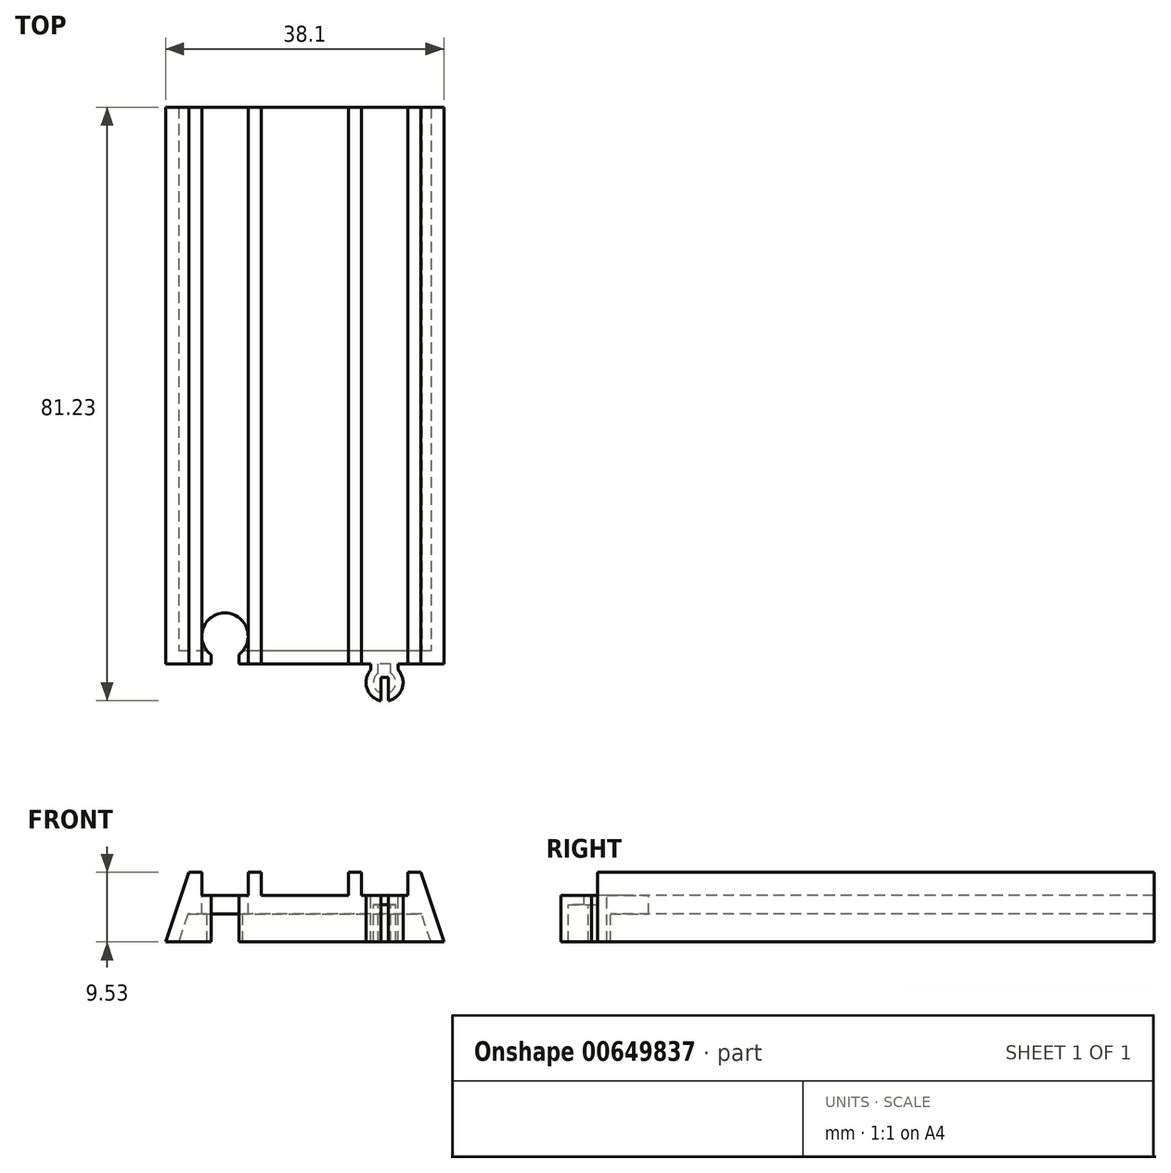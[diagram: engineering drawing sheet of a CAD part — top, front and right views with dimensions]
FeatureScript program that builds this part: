
annotation { "Feature Type Name" : "Feature", "Feature Type Description" : "" }
export const myFeature = defineFeature(function(context is Context, id is Id, definition is map)
    precondition{}
    {
        {
            var Q0;
            Q0=qCreatedBy(makeId("Front.planeOp"),FACE);
            var sketch = newSketch(context, id + "F0", { "sketchPlane" : qUnion([Q0])});
            skLineSegment(sketch, "E0", {"start": v(-19.05, 0) * mm, "end": v(-15.88, 9.52) * mm});
            skLineSegment(sketch, "E1", {"start": v(-15.88, 9.52) * mm, "end": v(15.88, 9.53) * mm});
            skLineSegment(sketch, "E2", {"start": v(15.88, 9.52) * mm, "end": v(19.05, 0) * mm});
            skLineSegment(sketch, "E3", {"start": v(19.05, 0) * mm, "end": v(-19.05, 0) * mm});
            skSolve(sketch);
        }
        {
            var Q0;
            Q0 = qSketchRegion(id + "F0", true);
            extrude(context, id + "F1", {"entities" : qUnion([Q0]), "depth" : 76.2 * mm, "offsetDistance" : 25.4 * mm});
        }
        {
            var Q0;
            Q0=makeQuery(id+"F1.opExtrude","CAP_FACE",FACE,{"disambiguationData":[OSD([sQuery(id+"F0.wireOp",EDGE,"E0"),sQuery(id+"F0.wireOp",EDGE,"E1"),sQuery(id+"F0.wireOp",EDGE,"E2"),sQuery(id+"F0.wireOp",EDGE,"E3")])],"isStart":false});
            var sketch = newSketch(context, id + "F2", { "sketchPlane" : qUnion([Q0])});
            skLineSegment(sketch, "E4.bottom", {"start": v(-14.1, 9.52) * mm, "end": v(-7.75, 9.52) * mm});
            skLineSegment(sketch, "E4.top", {"start": v(-14.1, 6.35) * mm, "end": v(-7.75, 6.35) * mm});
            skLineSegment(sketch, "E4.left", {"start": v(-14.1, 9.52) * mm, "end": v(-14.1, 6.35) * mm});
            skLineSegment(sketch, "E4.right", {"start": v(-7.75, 9.52) * mm, "end": v(-7.75, 6.35) * mm});
            skLineSegment(sketch, "E5.bottom", {"start": v(7.75, 9.52) * mm, "end": v(14.1, 9.52) * mm});
            skLineSegment(sketch, "E5.top", {"start": v(7.75, 6.35) * mm, "end": v(14.1, 6.35) * mm});
            skLineSegment(sketch, "E5.left", {"start": v(7.75, 9.52) * mm, "end": v(7.75, 6.35) * mm});
            skLineSegment(sketch, "E5.right", {"start": v(14.1, 9.52) * mm, "end": v(14.1, 6.35) * mm});
            skPoint(sketch, "E6", {"position": v(-15.88, 9.52) * mm});
            skLineSegment(sketch, "E7.bottom", {"start": v(-5.97, 9.52) * mm, "end": v(5.97, 9.52) * mm});
            skLineSegment(sketch, "E7.top", {"start": v(-5.97, 6.35) * mm, "end": v(5.97, 6.35) * mm});
            skLineSegment(sketch, "E7.left", {"start": v(-5.97, 9.52) * mm, "end": v(-5.97, 6.35) * mm});
            skLineSegment(sketch, "E7.right", {"start": v(5.97, 9.52) * mm, "end": v(5.97, 6.35) * mm});
            skPoint(sketch, "E8", {"position": v(15.88, 9.53) * mm});
            skLineSegment(sketch, "E9", {"start": v(-17.27, 0) * mm, "end": v(-16, 3.8) * mm});
            skLineSegment(sketch, "E10", {"start": v(-16, 3.8) * mm, "end": v(16, 3.8) * mm});
            skLineSegment(sketch, "E11", {"start": v(16, 3.8) * mm, "end": v(17.27, 0) * mm});
            skLineSegment(sketch, "E12", {"start": v(17.27, 0) * mm, "end": v(-17.27, 0) * mm});
            skLineSegment(sketch, "E13", {"start": v(-15.88, 9.52) * mm, "end": v(-14.1, 9.52) * mm, "construction": true});
            skLineSegment(sketch, "E14", {"start": v(-7.75, 9.52) * mm, "end": v(-5.97, 9.52) * mm});
            skLineSegment(sketch, "E15", {"start": v(5.97, 9.52) * mm, "end": v(7.75, 9.52) * mm});
            skLineSegment(sketch, "E16", {"start": v(14.1, 9.52) * mm, "end": v(15.88, 9.52) * mm});
            skLineSegment(sketch, "E17", {"start": v(-17.27, 0) * mm, "end": v(-19.05, 0) * mm, "construction": true});
            skLineSegment(sketch, "E18", {"start": v(17.27, 0) * mm, "end": v(19.05, 0) * mm, "construction": true});
            skSolve(sketch);
        }
        {
            var Q0;
            Q0 = qSketchRegion(id + "F2", true);
            extrude(context, id + "F3", {"entities" : qUnion([Q0]), "operationType" : NewBodyOperationType.REMOVE, "endBound" : BoundingType.THROUGH_ALL, "oppositeDirection" : true, "depth" : 25.4 * mm, "offsetDistance" : 25.4 * mm});
        }
        {
            var Q0;
            Q0=makeQuery(id+"F1.opExtrude","CAP_FACE",FACE,{"disambiguationData":[OSD([sQuery(id+"F0.wireOp",EDGE,"E0"),sQuery(id+"F0.wireOp",EDGE,"E1"),sQuery(id+"F0.wireOp",EDGE,"E2"),sQuery(id+"F0.wireOp",EDGE,"E3")])],"isStart":false});
            var sketch = newSketch(context, id + "F4", { "sketchPlane" : qUnion([Q0])});
            skLineSegment(sketch, "E19", {"start": v(-19.05, 0) * mm, "end": v(-15.88, 9.52) * mm});
            skLineSegment(sketch, "E20", {"start": v(-15.88, 9.52) * mm, "end": v(-14.1, 9.52) * mm});
            skLineSegment(sketch, "E21", {"start": v(15.88, 9.52) * mm, "end": v(19.05, 0) * mm});
            skLineSegment(sketch, "E22", {"start": v(19.05, 0) * mm, "end": v(-19.05, 0) * mm});
            skLineSegment(sketch, "E23", {"start": v(-14.1, 9.52) * mm, "end": v(-14.1, 6.35) * mm});
            skLineSegment(sketch, "E24", {"start": v(-14.1, 6.35) * mm, "end": v(-7.75, 6.35) * mm});
            skLineSegment(sketch, "E25", {"start": v(-7.75, 6.35) * mm, "end": v(-7.75, 9.52) * mm});
            skLineSegment(sketch, "E26.trimOffspring", {"start": v(-7.75, 9.52) * mm, "end": v(-5.97, 9.52) * mm});
            skLineSegment(sketch, "E27.bottom", {"start": v(7.75, 6.35) * mm, "end": v(14.1, 6.35) * mm});
            skLineSegment(sketch, "E27.left", {"start": v(7.75, 6.35) * mm, "end": v(7.75, 9.52) * mm});
            skLineSegment(sketch, "E27.right", {"start": v(14.1, 6.35) * mm, "end": v(14.1, 9.53) * mm});
            skLineSegment(sketch, "E28.trimOffspring", {"start": v(14.1, 9.53) * mm, "end": v(15.88, 9.53) * mm});
            skLineSegment(sketch, "E29", {"start": v(-5.97, 6.35) * mm, "end": v(5.97, 6.35) * mm});
            skLineSegment(sketch, "E30", {"start": v(5.97, 6.35) * mm, "end": v(5.97, 9.52) * mm});
            skLineSegment(sketch, "E31", {"start": v(5.97, 9.52) * mm, "end": v(7.75, 9.52) * mm});
            skLineSegment(sketch, "E32", {"start": v(-5.97, 9.52) * mm, "end": v(-5.97, 6.35) * mm});
            skSolve(sketch);
        }
        {
            var Q0;
            Q0 = qSketchRegion(id + "F4", true);
            extrude(context, id + "F5", {"entities" : qUnion([Q0]), "operationType" : NewBodyOperationType.ADD, "oppositeDirection" : true, "depth" : 1.78 * mm, "offsetDistance" : 25.4 * mm});
        }
        {
            var Q0;
            Q0=makeQuery(id+"F3.boolean.opBoolean","COPY",FACE,{"derivedFrom":makeQuery(id+"F3.opExtrude","SWEPT_FACE",FACE,{"disambiguationData":[OSD([sQuery(id+"F2.wireOp",EDGE,"E10")])]})});
            var sketch = newSketch(context, id + "F6", { "sketchPlane" : qUnion([Q0])});
            skArc(sketch, "E33", {"start": v(-13.36, 74.42) * mm, "mid": v(-10.92, 69.22) * mm, "end": v(-8.48, 74.42) * mm});
            skLineSegment(sketch, "E34", {"start": v(-10.92, 76.2) * mm, "end": v(-10.92, 72.4) * mm, "construction": true});
            skSolve(sketch);
        }
        {
            var Q0;
            Q0=makeQuery(id+"F6.imprint","IMPRINT",FACE,{"disambiguationData":[TD([[makeQuery(id+"F6.imprint","IMPRINT",EDGE,{"derivedFrom":sQuery(id+"F6.wireOp",EDGE,"E33")}),1.0]])]});
            var Q1;
            {var subQ0=sQuery(id+"F0.wireOp",EDGE,"E3");var subQ1=sQuery(id+"F0.wireOp",EDGE,"E2");var subQ3=sQuery(id+"F0.wireOp",EDGE,"E0");var subQ6=makeQuery(id+"F1.opExtrude","SWEPT_FACE",FACE,{"disambiguationData":[OSD([subQ0])]});Q1=makeQuery(id+"F5.boolean.opBoolean","MERGE",FACE,{"derivedFrom":[makeQuery(id+"F3.boolean.opBoolean","SPLIT",FACE,{"disambiguationData":[TD([makeQuery(id+"F1.opExtrude","SWEPT_FACE",FACE,{"disambiguationData":[OSD([subQ3])]})])],"derivedFrom":subQ6}),makeQuery(id+"F3.boolean.opBoolean","SPLIT",FACE,{"disambiguationData":[TD([makeQuery(id+"F1.opExtrude","SWEPT_FACE",FACE,{"disambiguationData":[OSD([subQ1])]})])],"derivedFrom":subQ6}),makeQuery(id+"F5.opExtrude","SWEPT_FACE",FACE,{"disambiguationData":[OSD([sQuery(id+"F4.wireOp",EDGE,"E22")])]})]});}
            extrude(context, id + "F7", {"entities" : qUnion([Q0]), "operationType" : NewBodyOperationType.ADD, "endBound" : BoundingType.UP_TO_SURFACE, "depth" : 25.4 * mm, "endBoundEntityFace" : qUnion([Q1]), "offsetDistance" : 25.4 * mm});
        }
        {
            var Q0;
            Q0=makeQuery(id+"F3.boolean.opBoolean","COPY",FACE,{"derivedFrom":makeQuery(id+"F3.opExtrude","SWEPT_FACE",FACE,{"disambiguationData":[OSD([sQuery(id+"F2.wireOp",EDGE,"E4.top")])]})});
            var sketch = newSketch(context, id + "F8", { "sketchPlane" : qUnion([Q0])});
            skArc(sketch, "E35", {"start": v(-9.02, -74.93) * mm, "mid": v(-10.92, -69.22) * mm, "end": v(-12.83, -74.93) * mm});
            skLineSegment(sketch, "E36", {"start": v(-12.83, -74.93) * mm, "end": v(-12.83, -76.2) * mm});
            skLineSegment(sketch, "E37", {"start": v(-9.02, -74.93) * mm, "end": v(-9.02, -76.2) * mm});
            skLineSegment(sketch, "E38", {"start": v(-9.02, -76.2) * mm, "end": v(-12.83, -76.2) * mm});
            skLineSegment(sketch, "E39", {"start": v(-9.02, -76.2) * mm, "end": v(-7.75, -76.2) * mm, "construction": true});
            skLineSegment(sketch, "E40", {"start": v(-12.83, -76.2) * mm, "end": v(-14.1, -76.2) * mm, "construction": true});
            skSolve(sketch);
        }
        {
            var Q0;
            Q0 = qSketchRegion(id + "F8", true);
            extrude(context, id + "F9", {"entities" : qUnion([Q0]), "operationType" : NewBodyOperationType.REMOVE, "endBound" : BoundingType.THROUGH_ALL, "oppositeDirection" : true, "depth" : 25.4 * mm, "offsetDistance" : 25.4 * mm});
        }
        {
            var Q0;
            Q0=makeQuery(id+"F3.boolean.opBoolean","COPY",FACE,{"derivedFrom":makeQuery(id+"F3.opExtrude","SWEPT_FACE",FACE,{"disambiguationData":[OSD([sQuery(id+"F2.wireOp",EDGE,"E5.top")])]})});
            var sketch = newSketch(context, id + "F10", { "sketchPlane" : qUnion([Q0])});
            skArc(sketch, "E41", {"start": v(9.04, -77.04) * mm, "mid": v(8.5, -79.53) * mm, "end": v(10.41, -81.23) * mm});
            skLineSegment(sketch, "E42", {"start": v(10.92, -76.2) * mm, "end": v(10.92, -78.74) * mm, "construction": true});
            skLineSegment(sketch, "E43", {"start": v(9.04, -77.04) * mm, "end": v(9.04, -76.2) * mm});
            skLineSegment(sketch, "E44", {"start": v(9.04, -76.2) * mm, "end": v(12.8, -76.2) * mm});
            skLineSegment(sketch, "E45", {"start": v(12.8, -76.2) * mm, "end": v(12.8, -77.04) * mm});
            skLineSegment(sketch, "E46", {"start": v(10.41, -81.23) * mm, "end": v(10.41, -78.05) * mm});
            skLineSegment(sketch, "E47", {"start": v(10.41, -78.05) * mm, "end": v(11.43, -78.05) * mm});
            skLineSegment(sketch, "E48", {"start": v(11.43, -78.05) * mm, "end": v(11.43, -81.23) * mm});
            skArc(sketch, "E49.trimOffspring", {"start": v(11.43, -81.23) * mm, "mid": v(13.34, -79.53) * mm, "end": v(12.8, -77.04) * mm});
            skSolve(sketch);
        }
        {
            var Q0;
            Q0=makeQuery(id+"F10.imprint","IMPRINT",FACE,{"disambiguationData":[TD([[makeQuery(id+"F10.imprint","IMPRINT",EDGE,{"derivedFrom":sQuery(id+"F10.wireOp",EDGE,"E41")}),1.0]])]});
            extrude(context, id + "F11", {"entities" : qUnion([Q0]), "operationType" : NewBodyOperationType.ADD, "oppositeDirection" : true, "depth" : 1.27 * mm, "offsetDistance" : 25.4 * mm});
        }
        {
            var Q0;
            Q0=makeQuery(id+"F11.opExtrude","CAP_FACE",FACE,{"disambiguationData":[OSD([sQuery(id+"F10.wireOp",EDGE,"E41"),sQuery(id+"F10.wireOp",EDGE,"E43"),sQuery(id+"F10.wireOp",EDGE,"E44"),sQuery(id+"F10.wireOp",EDGE,"E45"),sQuery(id+"F10.wireOp",EDGE,"E46"),sQuery(id+"F10.wireOp",EDGE,"E47"),sQuery(id+"F10.wireOp",EDGE,"E48"),sQuery(id+"F10.wireOp",EDGE,"E49.trimOffspring")])],"isStart":false});
            var sketch = newSketch(context, id + "F12", { "sketchPlane" : qUnion([Q0])});
            skArc(sketch, "E50", {"start": v(12.8, 77.04) * mm, "mid": v(13.34, 79.53) * mm, "end": v(11.43, 81.23) * mm});
            skLineSegment(sketch, "E51", {"start": v(9.04, 77.04) * mm, "end": v(9.04, 76.2) * mm});
            skLineSegment(sketch, "E52", {"start": v(9.04, 76.2) * mm, "end": v(10.05, 76.2) * mm});
            skLineSegment(sketch, "E53", {"start": v(12.8, 76.2) * mm, "end": v(12.8, 77.04) * mm});
            skArc(sketch, "E54", {"start": v(11.79, 77.49) * mm, "mid": v(12.43, 78.94) * mm, "end": v(11.43, 80.18) * mm});
            skLineSegment(sketch, "E55", {"start": v(10.05, 77.49) * mm, "end": v(10.05, 76.2) * mm});
            skLineSegment(sketch, "E56", {"start": v(11.79, 77.49) * mm, "end": v(11.79, 76.2) * mm});
            skLineSegment(sketch, "E57.trimOffspring", {"start": v(11.79, 76.2) * mm, "end": v(12.8, 76.2) * mm});
            skLineSegment(sketch, "E58", {"start": v(10.41, 81.23) * mm, "end": v(10.41, 80.18) * mm});
            skLineSegment(sketch, "E59", {"start": v(11.43, 81.23) * mm, "end": v(11.43, 80.18) * mm});
            skArc(sketch, "E60.trimOffspring", {"start": v(10.41, 80.18) * mm, "mid": v(9.41, 78.94) * mm, "end": v(10.05, 77.49) * mm});
            skArc(sketch, "E61.trimOffspring", {"start": v(10.41, 81.23) * mm, "mid": v(8.5, 79.53) * mm, "end": v(9.04, 77.04) * mm});
            skSolve(sketch);
        }
        {
            var Q0;
            Q0 = qSketchRegion(id + "F12", true);
            var Q1;
            {var subQ0=sQuery(id+"F4.wireOp",EDGE,"E22");var subQ1=sQuery(id+"F0.wireOp",EDGE,"E3");var subQ2=sQuery(id+"F0.wireOp",EDGE,"E2");var subQ4=sQuery(id+"F0.wireOp",EDGE,"E0");var subQ7=makeQuery(id+"F1.opExtrude","SWEPT_FACE",FACE,{"disambiguationData":[OSD([subQ1])]});Q1=makeQuery(id+"F7.boolean.opBoolean","MERGE",FACE,{"derivedFrom":[makeQuery(id+"F5.boolean.opBoolean","MERGE",FACE,{"derivedFrom":[makeQuery(id+"F3.boolean.opBoolean","SPLIT",FACE,{"disambiguationData":[TD([makeQuery(id+"F1.opExtrude","SWEPT_FACE",FACE,{"disambiguationData":[OSD([subQ4])]})])],"derivedFrom":subQ7}),makeQuery(id+"F3.boolean.opBoolean","SPLIT",FACE,{"disambiguationData":[TD([makeQuery(id+"F1.opExtrude","SWEPT_FACE",FACE,{"disambiguationData":[OSD([subQ2])]})])],"derivedFrom":subQ7}),makeQuery(id+"F5.opExtrude","SWEPT_FACE",FACE,{"disambiguationData":[OSD([subQ0])]})]}),makeQuery(id+"F7.opExtrude","CAP_FACE",FACE,{"disambiguationData":[OSD([subQ1,subQ0])],"isStart":false})]});}
            extrude(context, id + "F13", {"entities" : qUnion([Q0]), "operationType" : NewBodyOperationType.ADD, "endBound" : BoundingType.UP_TO_SURFACE, "depth" : 25.4 * mm, "endBoundEntityFace" : qUnion([Q1]), "offsetDistance" : 25.4 * mm});
        }
    });
